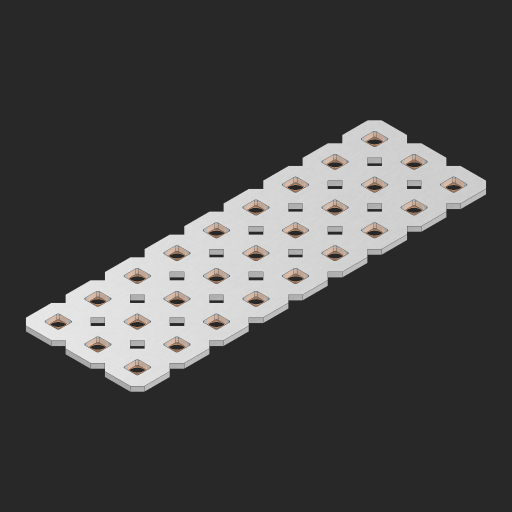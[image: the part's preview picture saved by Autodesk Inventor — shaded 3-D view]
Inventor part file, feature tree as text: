
AUTODESK INVENTOR PART (.ipt)
format: ipt  version: 2023 (Build 270158000, 158)  size: 598,528 bytes
history: native  units: in
note: dims shown in document units (in); Inventor stores cm internally (conversion verified against a paired STEP export)
features: other x28, extrude x26, sketch x2, pattern_linear x1
ambient origin geometry x8: Origin, YZ Plane, XZ Plane, XY Plane, X Axis, Y Axis, Z Axis, Center Point
bodies: Solid1 (feature_tree), Body (feature_tree)
feature tree (57):
  pattern_linear  "Rectangular Pattern1"  Spacing1=0.09in  [1 undecoded]
  sketch  "Sketch1"  dims[d1=0.5in]
  sketch  "Sketch2"  dims[d2=0.182in d3=0.09in d4=0.09in d5=0.09in d6=0.09in d7=0.09in d8=0.09in d9=0.09in d10=0.09in d11=0.02in d13=0.0in d14=0.172in d15=0.0625in d16=0.0in d19=0.5in d22=0.5in]
  other  "Srf1"
  other  "Srf126"
  other  "Srf127"
  other  "Srf128"
  other  "Srf129"
  other  "Srf130"
  other  "Srf131"
  other  "Srf250"
  other  "Srf251"
  other  "Srf268"
  other  "Srf269"
  other  "Srf270"
  other  "Srf271"
  other  "Srf272"
  other  "Srf273"
  other  "Srf274"
  other  "Srf275"
  other  "Srf276"
  other  "Srf293"
  other  "Srf294"
  other  "Srf295"
  other  "Srf296"
  other  "Srf297"
  other  "Srf298"
  other  "Srf299"
  other  "Srf300"
  other  "Srf301"
  other  "Circle"
  extrude  "ExtrusionSrf126"  Depth=0.09in
  extrude  "ExtrusionSrf127"  Depth=0.09in
  extrude  "ExtrusionSrf128"  Depth=0.09in
  extrude  "ExtrusionSrf129"  Depth=0.09in
  extrude  "ExtrusionSrf130"  Depth=0.09in
  extrude  "ExtrusionSrf131"  Depth=0.09in
  extrude  "ExtrusionSrf250"  Depth=0.09in
  extrude  "ExtrusionSrf251"  Depth=0.02in
  extrude  "ExtrusionSrf268"  TaperAngle=0.0deg  [1 undecoded]
  extrude  "ExtrusionSrf269"  Depth=0.5in
  extrude  "ExtrusionSrf270"  Depth=0.0625in TaperAngle=0.0deg
  extrude  "ExtrusionSrf271"  Depth=0.5in
  extrude  "ExtrusionSrf272"  Depth=0.5in
  extrude  "ExtrusionSrf273"  [1 undecoded]
  extrude  "ExtrusionSrf274"  [1 undecoded]
  extrude  "ExtrusionSrf275"  [1 undecoded]
  extrude  "ExtrusionSrf276"  [1 undecoded]
  extrude  "ExtrusionSrf293"  [1 undecoded]
  extrude  "ExtrusionSrf294"  [1 undecoded]
  extrude  "ExtrusionSrf295"  [1 undecoded]
  extrude  "ExtrusionSrf296"  [1 undecoded]
  extrude  "ExtrusionSrf297"  [1 undecoded]
  extrude  "ExtrusionSrf298"  [1 undecoded]
  extrude  "ExtrusionSrf299"  [1 undecoded]
  extrude  "ExtrusionSrf300"  [1 undecoded]
  extrude  "ExtrusionSrf301"  [1 undecoded]
note: 15 required parameter values undecoded (feature->parameter linkage not recoverable at this tier; creation-order binding heuristic only, values carry confidence <= 0.55)
